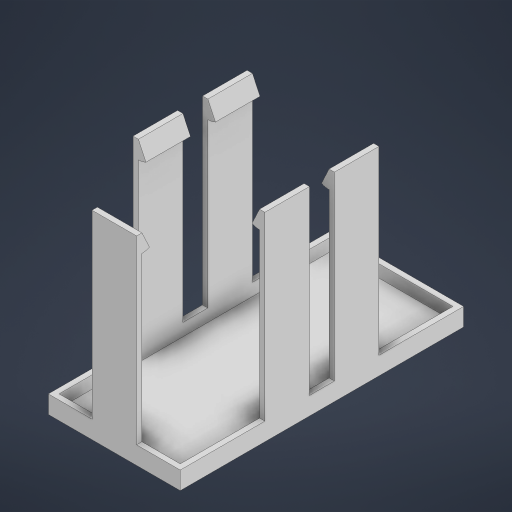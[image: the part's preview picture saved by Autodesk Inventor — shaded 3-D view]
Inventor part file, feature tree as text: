
AUTODESK INVENTOR PART (.ipt)
format: ipt  version: 2023 (Build 270158000, 158)  size: 282,112 bytes
history: native  units: mm
features: sketch x6, extrude x3, revolve x3
ambient origin geometry x8: Origin, YZ Plane, XZ Plane, XY Plane, X Axis, Y Axis, Z Axis, Center Point
bodies: Solid1 (feature_tree)
feature tree (12):
  extrude  "Extrusion1"  Depth=159.0mm
  extrude  "Extrusion2"  Depth=3.0mm
  sketch  "Sketch3"  dims[d5=3.0mm d6=7.0mm]
  sketch  "Sketch4"  dims[d7=7.0mm d8=32.0mm]
  revolve  "Revolution1"  [1 undecoded]
  revolve  "Revolution2"  [1 undecoded]
  revolve  "Revolution3"  [1 undecoded]
  extrude  "Extrusion3"  Depth=108.5mm TaperAngle=0.0deg
  sketch  "Sketch1"  dims[d0=74.0mm d1=159.0mm]
  sketch  "Sketch2"  dims[d2=3.0mm d3=0.0mm d4=3.0mm]
  sketch  "Sketch5"  dims[d9=32.0mm d10=12.5mm]
  sketch  "Sketch6"  dims[d11=12.5mm d12=108.5mm d13=0.0mm d14=25.0mm d15=10.0mm d16=25.0mm d17=10.0mm d18=25.0mm d19=10.0mm d20=25.0mm d21=10.0mm d22=25.0mm d23=10.0mm d24=4.363323mm d25=4.363323mm d26=4.363323mm d27=3.0mm d28=3.0mm d29=3.0mm d30=3.0mm d31=7.0mm d32=0.0mm]
note: 3 required parameter values undecoded (feature->parameter linkage not recoverable at this tier; creation-order binding heuristic only, values carry confidence <= 0.55)
